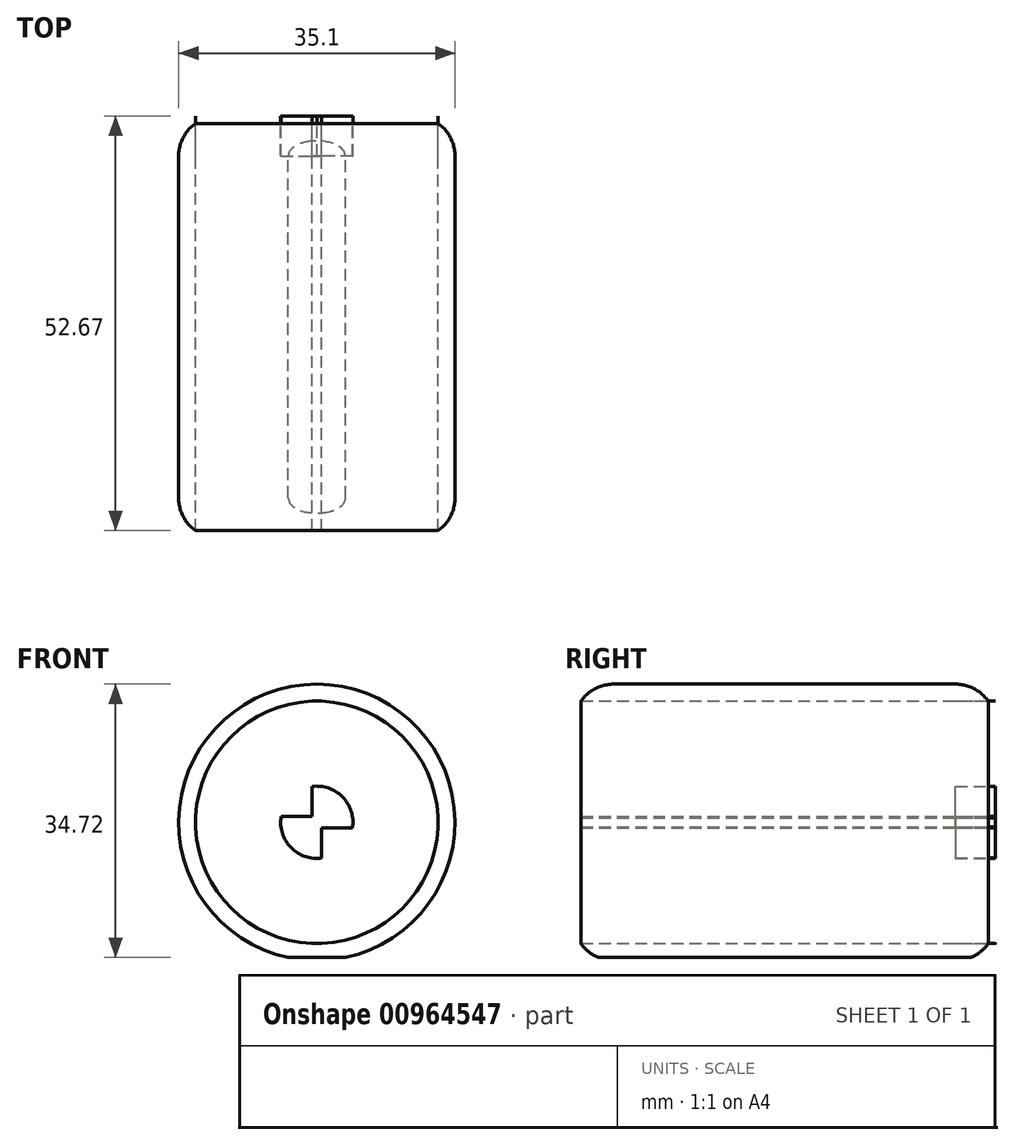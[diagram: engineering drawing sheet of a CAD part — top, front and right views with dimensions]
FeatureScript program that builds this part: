
annotation { "Feature Type Name" : "Feature", "Feature Type Description" : "" }
export const myFeature = defineFeature(function(context is Context, id is Id, definition is map)
    precondition{}
    {
        {
            var Q0;
            Q0=qCreatedBy(makeId("Front.planeOp"),FACE);
            var sketch = newSketch(context, id + "F0", { "sketchPlane" : qUnion([Q0])});
            skCircle(sketch, "E0", {"center": v(0, 0) * mm, "radius": 17.55 * mm});
            skCircle(sketch, "E1", {"center": v(0, 0) * mm, "radius": 15.4 * mm});
            skLineSegment(sketch, "E2", {"start": v(0, -15.4) * mm, "end": v(-0.63, -15.4) * mm});
            skLineSegment(sketch, "E3", {"start": v(-0.63, -15.4) * mm, "end": v(-0.63, 15.4) * mm});
            skLineSegment(sketch, "E4", {"start": v(-0.63, 15.4) * mm, "end": v(0.63, 15.4) * mm});
            skLineSegment(sketch, "E5", {"start": v(0.63, 15.4) * mm, "end": v(0.63, -15.4) * mm});
            skLineSegment(sketch, "E6", {"start": v(0.63, -15.4) * mm, "end": v(0, -15.4) * mm});
            skLineSegment(sketch, "E7", {"start": v(-15.39, 0.72) * mm, "end": v(15.39, 0.72) * mm});
            skLineSegment(sketch, "E8", {"start": v(15.39, 0.72) * mm, "end": v(15.39, -0.72) * mm});
            skLineSegment(sketch, "E9", {"start": v(15.39, -0.72) * mm, "end": v(-15.39, -0.72) * mm});
            skLineSegment(sketch, "E10", {"start": v(-15.39, -0.72) * mm, "end": v(-15.39, 0.72) * mm});
            skCircle(sketch, "E11", {"center": v(0, 0) * mm, "radius": 4.59 * mm});
            skCircle(sketch, "E12", {"center": v(0, 0) * mm, "radius": 3.7 * mm});
            skLineSegment(sketch, "E13", {"start": v(-12.06, -12.75) * mm, "end": v(-12.06, -21.8) * mm});
            skLineSegment(sketch, "E14", {"start": v(-12.06, -21.8) * mm, "end": v(0, -21.8) * mm});
            skLineSegment(sketch, "E15", {"start": v(0, -21.8) * mm, "end": v(0, -17.55) * mm});
            skLineSegment(sketch, "E16.MirrorCS", {"start": v(12.06, -12.75) * mm, "end": v(12.06, -21.8) * mm});
            skLineSegment(sketch, "E17.MirrorCS", {"start": v(12.06, -21.8) * mm, "end": v(0, -21.8) * mm});
            skSolve(sketch);
        }
        {
            var Q0;
            {var subQ16=sQuery(id+"F0.wireOp",EDGE,"E0");var subQ17=makeQuery(id+"F0.imprint","INTERSECT",VERTEX,{"derivedFrom":[subQ16,sQuery(id+"F0.wireOp",EDGE,"E13")]});Q0=makeQuery(id+"F0.imprint","IMPRINT",FACE,{"disambiguationData":[TD([[makeQuery(id+"F0.imprint","IMPRINT",EDGE,{"disambiguationData":[TD([[subQ17,-1.0]])],"derivedFrom":subQ16}),1.0]])]});}
            var Q1;
            {var subQ0=sQuery(id+"F0.wireOp",EDGE,"E15");Q1=makeQuery(id+"F0.imprint","IMPRINT",FACE,{"disambiguationData":[TD([[makeQuery(id+"F0.imprint","IMPRINT",EDGE,{"derivedFrom":subQ0}),-1.0]])]});}
            var Q2;
            {var subQ0=sQuery(id+"F0.wireOp",EDGE,"E13");Q2=makeQuery(id+"F0.imprint","IMPRINT",FACE,{"disambiguationData":[TD([[makeQuery(id+"F0.imprint","IMPRINT",EDGE,{"derivedFrom":subQ0}),1.0]])]});}
            extrude(context, id + "F1", {"entities" : qUnion([Q0, Q1, Q2]), "depth" : 53.6 * mm, "offsetDistance" : 25.4 * mm});
        }
        {
            var Q0;
            Q0=makeQuery(id+"F1.opExtrude","CAP_EDGE",EDGE,{"disambiguationData":[OSD([sQuery(id+"F0.wireOp",EDGE,"E0")])],"isStart":true});
            var Q1;
            Q1=makeQuery(id+"F1.opExtrude","CAP_EDGE",EDGE,{"disambiguationData":[OSD([sQuery(id+"F0.wireOp",EDGE,"E13")])],"isStart":false});
            var Q2;
            Q2=makeQuery(id+"F1.opExtrude","CAP_EDGE",EDGE,{"disambiguationData":[OSD([sQuery(id+"F0.wireOp",EDGE,"E16.MirrorCS")])],"isStart":false});
            var Q3;
            Q3=makeQuery(id+"F1.opExtrude","CAP_EDGE",EDGE,{"disambiguationData":[OSD([sQuery(id+"F0.wireOp",EDGE,"E0")])],"isStart":false});
            var Q4;
            Q4=makeQuery(id+"F1.opExtrude","CAP_EDGE",EDGE,{"disambiguationData":[OSD([sQuery(id+"F0.wireOp",EDGE,"E16.MirrorCS")])],"isStart":true});
            var Q5;
            Q5=makeQuery(id+"F1.opExtrude","CAP_EDGE",EDGE,{"disambiguationData":[OSD([sQuery(id+"F0.wireOp",EDGE,"E13")])],"isStart":true});
            fillet(context, id + "F2", {"entities" : qUnion([Q0, Q1, Q2, Q3, Q4, Q5]), "radius" : 5.08 * mm, "tangentPropagation" : true, "allowEdgeOverflow" : false});
        }
        {
            var Q0;
            {var subQ0=sQuery(id+"F0.wireOp",EDGE,"E12");var subQ1=sQuery(id+"F0.wireOp",EDGE,"E7");var subQ2=makeQuery(id+"F0.imprint","INTERSECT",VERTEX,{"disambiguationData":[OD(1.0)],"derivedFrom":[subQ1,subQ0]});Q0=makeQuery(id+"F0.imprint","IMPRINT",FACE,{"disambiguationData":[TD([[makeQuery(id+"F0.imprint","IMPRINT",EDGE,{"disambiguationData":[TD([[subQ2,-1.0]])],"derivedFrom":subQ1}),-1.0]])]});}
            var Q1;
            {var subQ0=sQuery(id+"F0.wireOp",EDGE,"E11");var subQ1=sQuery(id+"F0.wireOp",EDGE,"E5");var subQ2=makeQuery(id+"F0.imprint","INTERSECT",VERTEX,{"disambiguationData":[OD(0.0)],"derivedFrom":[subQ1,subQ0]});Q1=makeQuery(id+"F0.imprint","IMPRINT",FACE,{"disambiguationData":[TD([[makeQuery(id+"F0.imprint","IMPRINT",EDGE,{"disambiguationData":[TD([[subQ2,-1.0]])],"derivedFrom":subQ1}),1.0]])]});}
            var Q2;
            {var subQ0=sQuery(id+"F0.wireOp",EDGE,"E7");var subQ1=sQuery(id+"F0.wireOp",EDGE,"E5");var subQ2=makeQuery(id+"F0.imprint","INTERSECT",VERTEX,{"derivedFrom":[subQ1,subQ0]});Q2=makeQuery(id+"F0.imprint","IMPRINT",FACE,{"disambiguationData":[TD([[makeQuery(id+"F0.imprint","IMPRINT",EDGE,{"disambiguationData":[TD([[subQ2,-1.0]])],"derivedFrom":subQ1}),1.0]])]});}
            var Q3;
            {var subQ0=sQuery(id+"F0.wireOp",EDGE,"E8");Q3=makeQuery(id+"F0.imprint","IMPRINT",FACE,{"disambiguationData":[TD([[makeQuery(id+"F0.imprint","IMPRINT",EDGE,{"derivedFrom":subQ0}),-1.0]])]});}
            var Q4;
            {var subQ0=sQuery(id+"F0.wireOp",EDGE,"E12");var subQ1=sQuery(id+"F0.wireOp",EDGE,"E5");var subQ2=makeQuery(id+"F0.imprint","INTERSECT",VERTEX,{"disambiguationData":[OD(1.0)],"derivedFrom":[subQ1,subQ0]});Q4=makeQuery(id+"F0.imprint","IMPRINT",FACE,{"disambiguationData":[TD([[makeQuery(id+"F0.imprint","IMPRINT",EDGE,{"disambiguationData":[TD([[subQ2,-1.0]])],"derivedFrom":subQ1}),1.0]])]});}
            var Q5;
            {var subQ0=sQuery(id+"F0.wireOp",EDGE,"E11");var subQ1=sQuery(id+"F0.wireOp",EDGE,"E3");var subQ2=makeQuery(id+"F0.imprint","INTERSECT",VERTEX,{"disambiguationData":[OD(0.0)],"derivedFrom":[subQ1,subQ0]});Q5=makeQuery(id+"F0.imprint","IMPRINT",FACE,{"disambiguationData":[TD([[makeQuery(id+"F0.imprint","IMPRINT",EDGE,{"disambiguationData":[TD([[subQ2,-1.0]])],"derivedFrom":subQ1}),-1.0]])]});}
            var Q6;
            {var subQ0=sQuery(id+"F0.wireOp",EDGE,"E12");var subQ1=sQuery(id+"F0.wireOp",EDGE,"E3");var subQ2=makeQuery(id+"F0.imprint","INTERSECT",VERTEX,{"disambiguationData":[OD(0.0)],"derivedFrom":[subQ1,subQ0]});Q6=makeQuery(id+"F0.imprint","IMPRINT",FACE,{"disambiguationData":[TD([[makeQuery(id+"F0.imprint","IMPRINT",EDGE,{"disambiguationData":[TD([[subQ2,-1.0]])],"derivedFrom":subQ1}),-1.0]])]});}
            var Q7;
            {var subQ0=sQuery(id+"F0.wireOp",EDGE,"E9");var subQ1=sQuery(id+"F0.wireOp",EDGE,"E3");var subQ2=makeQuery(id+"F0.imprint","INTERSECT",VERTEX,{"derivedFrom":[subQ1,subQ0]});Q7=makeQuery(id+"F0.imprint","IMPRINT",FACE,{"disambiguationData":[TD([[makeQuery(id+"F0.imprint","IMPRINT",EDGE,{"disambiguationData":[TD([[subQ2,-1.0]])],"derivedFrom":subQ1}),-1.0]])]});}
            var Q8;
            {var subQ0=sQuery(id+"F0.wireOp",EDGE,"E7");var subQ1=sQuery(id+"F0.wireOp",EDGE,"E3");var subQ2=makeQuery(id+"F0.imprint","INTERSECT",VERTEX,{"derivedFrom":[subQ1,subQ0]});Q8=makeQuery(id+"F0.imprint","IMPRINT",FACE,{"disambiguationData":[TD([[makeQuery(id+"F0.imprint","IMPRINT",EDGE,{"disambiguationData":[TD([[subQ2,-1.0]])],"derivedFrom":subQ1}),-1.0]])]});}
            var Q9;
            {var subQ0=sQuery(id+"F0.wireOp",EDGE,"E12");var subQ1=sQuery(id+"F0.wireOp",EDGE,"E3");var subQ2=makeQuery(id+"F0.imprint","INTERSECT",VERTEX,{"disambiguationData":[OD(1.0)],"derivedFrom":[subQ1,subQ0]});Q9=makeQuery(id+"F0.imprint","IMPRINT",FACE,{"disambiguationData":[TD([[makeQuery(id+"F0.imprint","IMPRINT",EDGE,{"disambiguationData":[TD([[subQ2,-1.0]])],"derivedFrom":subQ1}),-1.0]])]});}
            var Q10;
            {var subQ0=sQuery(id+"F0.wireOp",EDGE,"E4");Q10=makeQuery(id+"F0.imprint","IMPRINT",FACE,{"disambiguationData":[TD([[makeQuery(id+"F0.imprint","IMPRINT",EDGE,{"derivedFrom":subQ0}),-1.0]])]});}
            var Q11;
            {var subQ0=sQuery(id+"F0.wireOp",EDGE,"E12");var subQ1=sQuery(id+"F0.wireOp",EDGE,"E3");var subQ2=makeQuery(id+"F0.imprint","INTERSECT",VERTEX,{"disambiguationData":[OD(1.0)],"derivedFrom":[subQ1,subQ0]});Q11=makeQuery(id+"F0.imprint","IMPRINT",FACE,{"disambiguationData":[TD([[makeQuery(id+"F0.imprint","IMPRINT",EDGE,{"disambiguationData":[TD([[subQ2,-1.0]])],"derivedFrom":subQ1}),1.0]])]});}
            var Q12;
            {var subQ0=sQuery(id+"F0.wireOp",EDGE,"E11");var subQ1=sQuery(id+"F0.wireOp",EDGE,"E7");var subQ2=makeQuery(id+"F0.imprint","INTERSECT",VERTEX,{"disambiguationData":[OD(0.0)],"derivedFrom":[subQ1,subQ0]});Q12=makeQuery(id+"F0.imprint","IMPRINT",FACE,{"disambiguationData":[TD([[makeQuery(id+"F0.imprint","IMPRINT",EDGE,{"disambiguationData":[TD([[subQ2,-1.0]])],"derivedFrom":subQ1}),-1.0]])]});}
            var Q13;
            {var subQ0=sQuery(id+"F0.wireOp",EDGE,"E9");var subQ1=sQuery(id+"F0.wireOp",EDGE,"E3");var subQ2=makeQuery(id+"F0.imprint","INTERSECT",VERTEX,{"derivedFrom":[subQ1,subQ0]});Q13=makeQuery(id+"F0.imprint","IMPRINT",FACE,{"disambiguationData":[TD([[makeQuery(id+"F0.imprint","IMPRINT",EDGE,{"disambiguationData":[TD([[subQ2,-1.0]])],"derivedFrom":subQ1}),1.0]])]});}
            var Q14;
            {var subQ0=sQuery(id+"F0.wireOp",EDGE,"E10");Q14=makeQuery(id+"F0.imprint","IMPRINT",FACE,{"disambiguationData":[TD([[makeQuery(id+"F0.imprint","IMPRINT",EDGE,{"derivedFrom":subQ0}),-1.0]])]});}
            var Q15;
            {var subQ0=sQuery(id+"F0.wireOp",EDGE,"E11");var subQ1=sQuery(id+"F0.wireOp",EDGE,"E3");var subQ2=makeQuery(id+"F0.imprint","INTERSECT",VERTEX,{"disambiguationData":[OD(0.0)],"derivedFrom":[subQ1,subQ0]});Q15=makeQuery(id+"F0.imprint","IMPRINT",FACE,{"disambiguationData":[TD([[makeQuery(id+"F0.imprint","IMPRINT",EDGE,{"disambiguationData":[TD([[subQ2,-1.0]])],"derivedFrom":subQ1}),1.0]])]});}
            var Q16;
            {var subQ6=sQuery(id+"F0.wireOp",EDGE,"E2");Q16=makeQuery(id+"F0.imprint","IMPRINT",FACE,{"disambiguationData":[TD([[makeQuery(id+"F0.imprint","IMPRINT",EDGE,{"derivedFrom":subQ6}),-1.0]])]});}
            extrude(context, id + "F3", {"entities" : qUnion([Q0, Q1, Q2, Q3, Q4, Q5, Q6, Q7, Q8, Q9, Q10, Q11, Q12, Q13, Q14, Q15, Q16]), "depth" : 5.08 * mm, "offsetDistance" : 25.4 * mm});
        }
        {
            var Q0;
            Q0=qCreatedBy(makeId("Front.planeOp"),FACE);
            var sketch = newSketch(context, id + "F4", { "sketchPlane" : qUnion([Q0])});
            skLineSegment(sketch, "E18", {"start": v(0, -17.17) * mm, "end": v(-7.42, -17.17) * mm});
            skLineSegment(sketch, "E19", {"start": v(-7.42, -17.17) * mm, "end": v(-9.06, -18.35) * mm});
            skLineSegment(sketch, "E20", {"start": v(-9.06, -18.35) * mm, "end": v(-9.06, -20.08) * mm});
            skLineSegment(sketch, "E21", {"start": v(-9.06, -20.08) * mm, "end": v(-7.42, -20.08) * mm});
            skLineSegment(sketch, "E22", {"start": v(-7.42, -20.08) * mm, "end": v(-7.42, -22.01) * mm});
            skLineSegment(sketch, "E23", {"start": v(-7.42, -22.01) * mm, "end": v(0, -22.01) * mm});
            skLineSegment(sketch, "E24", {"start": v(0, -22.01) * mm, "end": v(0, -17.17) * mm});
            skLineSegment(sketch, "E25.MirrorCS", {"start": v(0, -17.17) * mm, "end": v(7.42, -17.17) * mm});
            skLineSegment(sketch, "E26.MirrorCS", {"start": v(7.42, -17.17) * mm, "end": v(9.06, -18.35) * mm});
            skLineSegment(sketch, "E27.MirrorCS", {"start": v(9.06, -18.35) * mm, "end": v(9.06, -20.08) * mm});
            skLineSegment(sketch, "E28.MirrorCS", {"start": v(9.06, -20.08) * mm, "end": v(7.42, -20.08) * mm});
            skLineSegment(sketch, "E29.MirrorCS", {"start": v(7.42, -20.08) * mm, "end": v(7.42, -22.01) * mm});
            skLineSegment(sketch, "E30.MirrorCS", {"start": v(7.42, -22.01) * mm, "end": v(0, -22.01) * mm});
            skSolve(sketch);
        }
        {
            var Q0;
            Q0=makeQuery(id+"F4.imprint","IMPRINT",FACE,{"disambiguationData":[TD([[makeQuery(id+"F4.imprint","IMPRINT",EDGE,{"derivedFrom":sQuery(id+"F4.wireOp",EDGE,"E18")}),1.0]])]});
            var Q1;
            Q1=makeQuery(id+"F4.imprint","IMPRINT",FACE,{"disambiguationData":[TD([[makeQuery(id+"F4.imprint","IMPRINT",EDGE,{"derivedFrom":sQuery(id+"F4.wireOp",EDGE,"E24")}),-1.0]])]});
            extrude(context, id + "F5", {"entities" : qUnion([Q0, Q1]), "operationType" : NewBodyOperationType.REMOVE, "depth" : 63 * mm, "offsetDistance" : 25.4 * mm});
        }
    });
